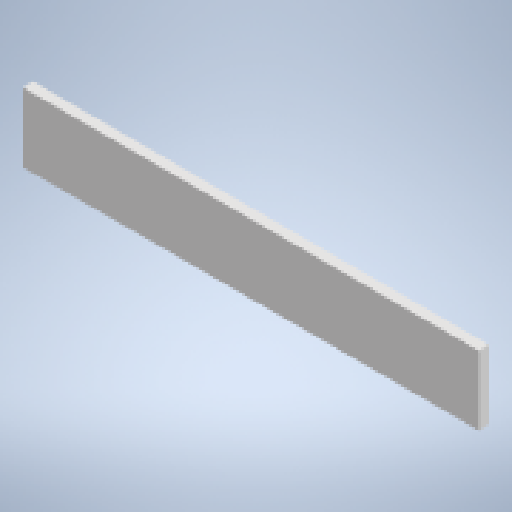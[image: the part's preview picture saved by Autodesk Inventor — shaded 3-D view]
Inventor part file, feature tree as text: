
AUTODESK INVENTOR PART (.ipt)
format: ipt  version: 2023 (Build 270158000, 158)  size: 138,240 bytes
history: native  units: mm
features: other x4, reference x2, extrude x1, sketch x1
ambient origin geometry x8: Origin, YZ Plane, XZ Plane, XY Plane, X Axis, Y Axis, Z Axis, Center Point
bodies: Solid1 (feature_tree)
feature tree (8):
  extrude  "Extrusion1"  Depth=20.0mm
  sketch  "Sketch1"  dims[d0=132.15mm d1=20.0mm d2=3.0mm d3=0.0mm]
  reference  "Reference1"
  reference  "Reference2"
  parser-record x1  (decoder bookkeeping rows leaked as tree rows — omitted from the tree; the rows remain in map.json)
  other  "Assembly.iam"
  other  "Album:1"
  other  "coverHolder:1"
note: 1 file-system path scrubbed to <path> (originals preserved in map.json)
